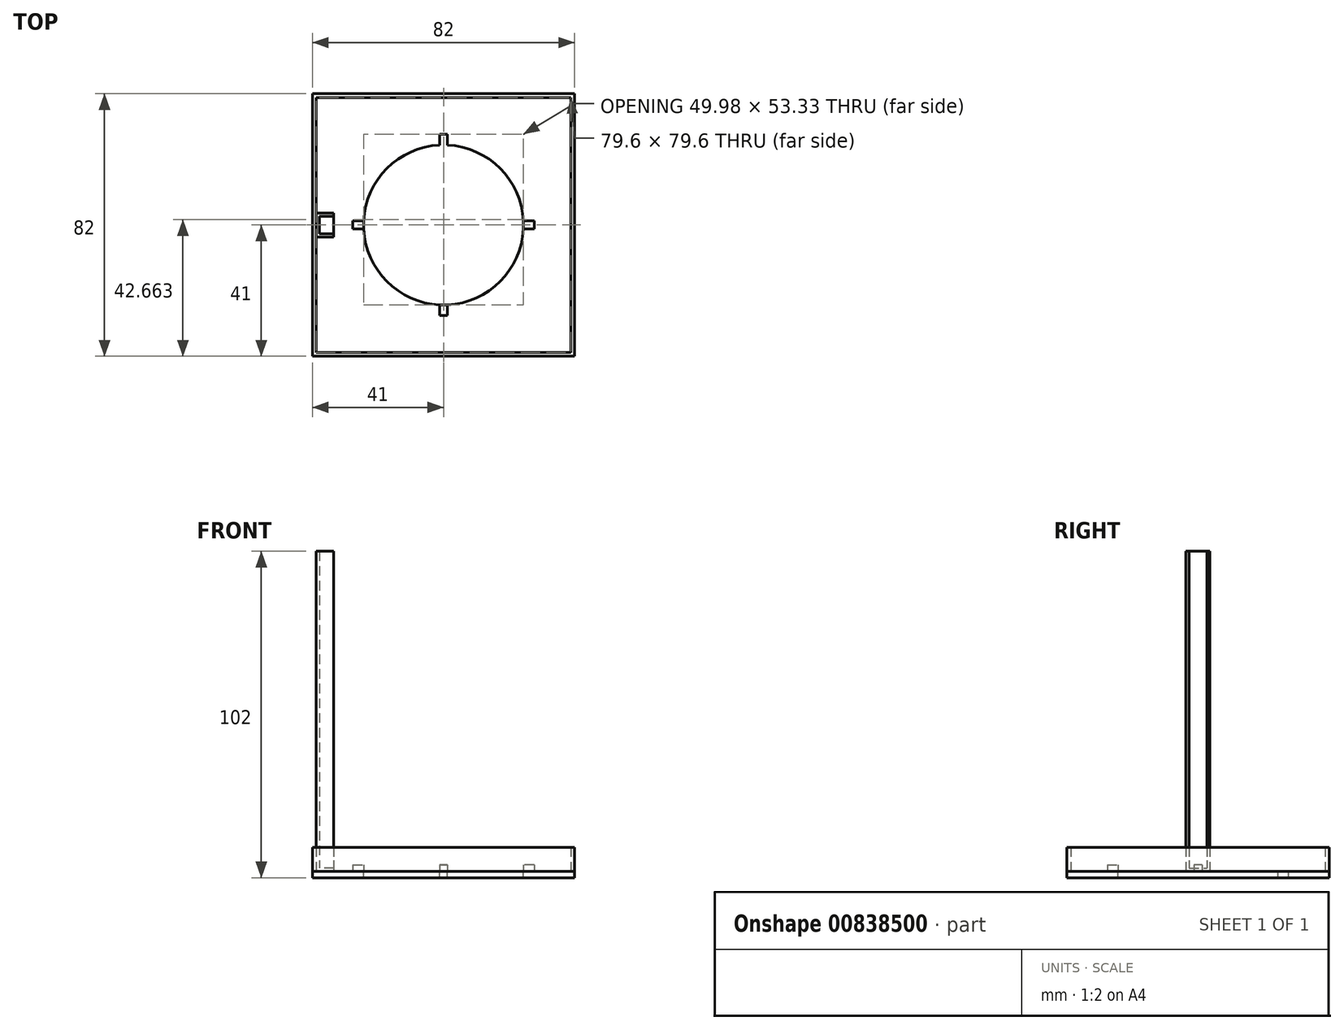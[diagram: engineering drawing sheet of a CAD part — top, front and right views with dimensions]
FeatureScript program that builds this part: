
annotation { "Feature Type Name" : "Feature", "Feature Type Description" : "" }
export const myFeature = defineFeature(function(context is Context, id is Id, definition is map)
    precondition{}
    {
        {
            var Q0;
            Q0=qCreatedBy(makeId("Top.planeOp"),FACE);
            var sketch = newSketch(context, id + "F0", { "sketchPlane" : qUnion([Q0])});
            skCircle(sketch, "E0", {"center": v(0, 0) * mm, "radius": 25 * mm});
            skCircle(sketch, "E1", {"center": v(0, 0) * mm, "radius": 32.8 * mm});
            skLineSegment(sketch, "E2.bottom", {"start": v(-1.25, 28.32) * mm, "end": v(1.25, 28.32) * mm});
            skLineSegment(sketch, "E2.top", {"start": v(-1.25, 21.68) * mm, "end": v(1.25, 21.68) * mm});
            skLineSegment(sketch, "E2.left", {"start": v(-1.25, 28.32) * mm, "end": v(-1.25, 21.68) * mm});
            skLineSegment(sketch, "E2.right", {"start": v(1.25, 28.32) * mm, "end": v(1.25, 21.68) * mm});
            skPoint(sketch, "E2.middle", {"position": v(0, 25) * mm});
            skLineSegment(sketch, "E3.bottom", {"start": v(28.33, 1.25) * mm, "end": v(21.68, 1.25) * mm});
            skLineSegment(sketch, "E3.top", {"start": v(28.33, -1.25) * mm, "end": v(21.68, -1.25) * mm});
            skLineSegment(sketch, "E3.left", {"start": v(28.33, 1.25) * mm, "end": v(28.33, -1.25) * mm});
            skLineSegment(sketch, "E3.right", {"start": v(21.68, 1.25) * mm, "end": v(21.68, -1.25) * mm});
            skPoint(sketch, "E3.middle", {"position": v(25, 0) * mm});
            skLineSegment(sketch, "E4.MirrorCS", {"start": v(1.25, 28.32) * mm, "end": v(-1.25, 28.32) * mm});
            skLineSegment(sketch, "E5.MirrorCS", {"start": v(1.25, 21.68) * mm, "end": v(-1.25, 21.68) * mm});
            skLineSegment(sketch, "E6.MirrorCS", {"start": v(-1.25, -21.68) * mm, "end": v(1.25, -21.68) * mm});
            skLineSegment(sketch, "E7.MirrorCS", {"start": v(-1.25, -28.32) * mm, "end": v(-1.25, -21.68) * mm});
            skLineSegment(sketch, "E8.MirrorCS", {"start": v(1.25, -28.32) * mm, "end": v(-1.25, -28.32) * mm});
            skLineSegment(sketch, "E9.MirrorCS", {"start": v(1.25, -28.32) * mm, "end": v(1.25, -21.68) * mm});
            skLineSegment(sketch, "E10.MirrorCS", {"start": v(-21.68, 1.25) * mm, "end": v(-21.68, -1.25) * mm});
            skLineSegment(sketch, "E11.MirrorCS", {"start": v(-28.33, 1.25) * mm, "end": v(-21.68, 1.25) * mm});
            skLineSegment(sketch, "E12.MirrorCS", {"start": v(-28.33, -1.25) * mm, "end": v(-21.68, -1.25) * mm});
            skLineSegment(sketch, "E13.MirrorCS", {"start": v(-28.33, 1.25) * mm, "end": v(-28.33, -1.25) * mm});
            skPoint(sketch, "E14.middle", {"position": v(-41.79, 0) * mm});
            skCircle(sketch, "E15", {"center": v(0, 0) * mm, "radius": 23.8 * mm});
            skLineSegment(sketch, "E16.bottom", {"start": v(-39.8, 39.8) * mm, "end": v(39.8, 39.8) * mm});
            skLineSegment(sketch, "E16.top", {"start": v(-39.8, -39.8) * mm, "end": v(39.8, -39.8) * mm});
            skLineSegment(sketch, "E16.left", {"start": v(-39.8, 39.8) * mm, "end": v(-39.8, -39.8) * mm});
            skLineSegment(sketch, "E16.right", {"start": v(39.8, 39.8) * mm, "end": v(39.8, -39.8) * mm});
            skLineSegment(sketch, "E17.bottom", {"start": v(-41, 41) * mm, "end": v(41, 41) * mm});
            skLineSegment(sketch, "E17.top", {"start": v(-41, -41) * mm, "end": v(41, -41) * mm});
            skLineSegment(sketch, "E17.left", {"start": v(-41, 41) * mm, "end": v(-41, -41) * mm});
            skLineSegment(sketch, "E17.right", {"start": v(41, 41) * mm, "end": v(41, -41) * mm});
            skLineSegment(sketch, "E18.bottom", {"start": v(-34.3, -3.75) * mm, "end": v(-39.8, -3.75) * mm});
            skLineSegment(sketch, "E18.top", {"start": v(-34.3, 3.75) * mm, "end": v(-39.8, 3.75) * mm});
            skLineSegment(sketch, "E18.left", {"start": v(-34.3, -3.75) * mm, "end": v(-34.3, 3.75) * mm});
            skLineSegment(sketch, "E18.right", {"start": v(-39.8, -3.75) * mm, "end": v(-39.8, 3.75) * mm});
            skPoint(sketch, "E18.middle", {"position": v(-37.05, 0) * mm});
            skSolve(sketch);
        }
        {
            var Q0;
            {var subQ0=sQuery(id+"F0.wireOp",EDGE,"E14.top");var subQ1=sQuery(id+"F0.wireOp",EDGE,"ETdMOg9K-giOR-L7Ai-rbHK-IAAoiEiWwUd0");var subQ2=makeQuery(id+"F0.imprint","INTERSECT",VERTEX,{"derivedFrom":[subQ1,subQ0]});Q0=makeQuery(id+"F0.imprint","IMPRINT",FACE,{"disambiguationData":[TD([[makeQuery(id+"F0.imprint","IMPRINT",EDGE,{"disambiguationData":[TD([[subQ2,1.0]])],"derivedFrom":subQ1}),-1.0]])]});}
            var Q1;
            {var subQ3=sQuery(id+"F0.wireOp",EDGE,"ETdMOg9K-giOR-L7Ai-rbHK-IAAoiEiWwUd0");var subQ5=makeQuery(id+"F0.imprint","INTERSECT",VERTEX,{"derivedFrom":[subQ3,sQuery(id+"F0.wireOp",EDGE,"7CK1xZji-ef6t-rpsp-r9yB-K5cPyd019NKb")]});Q1=makeQuery(id+"F0.imprint","IMPRINT",FACE,{"disambiguationData":[TD([[makeQuery(id+"F0.imprint","IMPRINT",EDGE,{"disambiguationData":[TD([[subQ5,1.0]])],"derivedFrom":subQ3}),-1.0]])]});}
            var Q2;
            {var subQ0=sQuery(id+"F0.wireOp",EDGE,"E7.MirrorCS");var subQ1=sQuery(id+"F0.wireOp",EDGE,"E0");var subQ2=makeQuery(id+"F0.imprint","INTERSECT",VERTEX,{"derivedFrom":[subQ1,subQ0]});Q2=makeQuery(id+"F0.imprint","IMPRINT",FACE,{"disambiguationData":[TD([[makeQuery(id+"F0.imprint","IMPRINT",EDGE,{"disambiguationData":[TD([[subQ2,-1.0]])],"derivedFrom":subQ1}),-1.0]])]});}
            var Q3;
            {var subQ0=sQuery(id+"F0.wireOp",EDGE,"E11.MirrorCS");var subQ1=sQuery(id+"F0.wireOp",EDGE,"E0");var subQ2=makeQuery(id+"F0.imprint","INTERSECT",VERTEX,{"derivedFrom":[subQ1,subQ0]});Q3=makeQuery(id+"F0.imprint","IMPRINT",FACE,{"disambiguationData":[TD([[makeQuery(id+"F0.imprint","IMPRINT",EDGE,{"disambiguationData":[TD([[subQ2,-1.0]])],"derivedFrom":subQ1}),-1.0]])]});}
            var Q4;
            {var subQ0=sQuery(id+"F0.wireOp",EDGE,"E2.right");var subQ1=sQuery(id+"F0.wireOp",EDGE,"E0");var subQ2=makeQuery(id+"F0.imprint","INTERSECT",VERTEX,{"derivedFrom":[subQ1,subQ0]});Q4=makeQuery(id+"F0.imprint","IMPRINT",FACE,{"disambiguationData":[TD([[makeQuery(id+"F0.imprint","IMPRINT",EDGE,{"disambiguationData":[TD([[subQ2,-1.0]])],"derivedFrom":subQ1}),-1.0]])]});}
            var Q5;
            {var subQ0=sQuery(id+"F0.wireOp",EDGE,"E9.MirrorCS");var subQ1=sQuery(id+"F0.wireOp",EDGE,"E0");var subQ2=makeQuery(id+"F0.imprint","INTERSECT",VERTEX,{"derivedFrom":[subQ1,subQ0]});Q5=makeQuery(id+"F0.imprint","IMPRINT",FACE,{"disambiguationData":[TD([[makeQuery(id+"F0.imprint","IMPRINT",EDGE,{"disambiguationData":[TD([[subQ2,1.0]])],"derivedFrom":subQ1}),-1.0]])]});}
            var Q6;
            {var subQ0=sQuery(id+"F0.wireOp",EDGE,"E2.left");var subQ1=sQuery(id+"F0.wireOp",EDGE,"E0");var subQ2=makeQuery(id+"F0.imprint","INTERSECT",VERTEX,{"derivedFrom":[subQ1,subQ0]});Q6=makeQuery(id+"F0.imprint","IMPRINT",FACE,{"disambiguationData":[TD([[makeQuery(id+"F0.imprint","IMPRINT",EDGE,{"disambiguationData":[TD([[subQ2,-1.0]])],"derivedFrom":subQ1}),-1.0]])]});}
            var Q7;
            {var subQ0=sQuery(id+"F0.wireOp",EDGE,"E9.MirrorCS");var subQ1=sQuery(id+"F0.wireOp",EDGE,"E0");var subQ2=makeQuery(id+"F0.imprint","INTERSECT",VERTEX,{"derivedFrom":[subQ1,subQ0]});Q7=makeQuery(id+"F0.imprint","IMPRINT",FACE,{"disambiguationData":[TD([[makeQuery(id+"F0.imprint","IMPRINT",EDGE,{"disambiguationData":[TD([[subQ2,-1.0]])],"derivedFrom":subQ1}),-1.0]])]});}
            var Q8;
            {var subQ0=sQuery(id+"F0.wireOp",EDGE,"E3.top");var subQ1=sQuery(id+"F0.wireOp",EDGE,"E0");var subQ2=makeQuery(id+"F0.imprint","INTERSECT",VERTEX,{"derivedFrom":[subQ1,subQ0]});Q8=makeQuery(id+"F0.imprint","IMPRINT",FACE,{"disambiguationData":[TD([[makeQuery(id+"F0.imprint","IMPRINT",EDGE,{"disambiguationData":[TD([[subQ2,1.0]])],"derivedFrom":subQ1}),-1.0]])]});}
            var Q9;
            {var subQ0=sQuery(id+"F0.wireOp",EDGE,"E12.MirrorCS");var subQ1=sQuery(id+"F0.wireOp",EDGE,"E0");var subQ2=makeQuery(id+"F0.imprint","INTERSECT",VERTEX,{"derivedFrom":[subQ1,subQ0]});Q9=makeQuery(id+"F0.imprint","IMPRINT",FACE,{"disambiguationData":[TD([[makeQuery(id+"F0.imprint","IMPRINT",EDGE,{"disambiguationData":[TD([[subQ2,-1.0]])],"derivedFrom":subQ1}),-1.0]])]});}
            var Q10;
            Q10=makeQuery(id+"F0.imprint","IMPRINT",FACE,{"disambiguationData":[TD([[makeQuery(id+"F0.imprint","IMPRINT",EDGE,{"derivedFrom":sQuery(id+"F0.wireOp",EDGE,"E16.bottom")}),1.0]])]});
            var Q11;
            Q11=sQuery(id+"F0.wireOp",EDGE,"ETdMOg9K-giOR-L7Ai-rbHK-IAAoiEiWwUd0");
            var Q12;
            Q12=sQuery(id+"F0.wireOp",EDGE,"E0");
            extrude(context, id + "F1", {"entities" : qUnion([Q0, Q1, Q2, Q3, Q4, Q5, Q6, Q7, Q8, Q9, Q10]), "surfaceEntities" : qUnion([Q11, Q12]), "depth" : 7.5 * mm, "offsetDistance" : 25 * mm});
        }
        {
            var Q0;
            Q0=makeQuery(id+"F0.imprint","IMPRINT",FACE,{"disambiguationData":[TD([[makeQuery(id+"F0.imprint","IMPRINT",EDGE,{"derivedFrom":sQuery(id+"F0.wireOp",EDGE,"E1")}),-1.0]])]});
            var Q1;
            Q1=makeQuery(id+"F0.imprint","IMPRINT",FACE,{"disambiguationData":[TD([[makeQuery(id+"F0.imprint","IMPRINT",EDGE,{"derivedFrom":sQuery(id+"F0.wireOp",EDGE,"E0")}),-1.0]])]});
            var Q2;
            Q2=makeQuery(id+"F0.imprint","IMPRINT",FACE,{"disambiguationData":[TD([[makeQuery(id+"F0.imprint","IMPRINT",EDGE,{"derivedFrom":sQuery(id+"F0.wireOp",EDGE,"7CK1xZji-ef6t-rpsp-r9yB-K5cPyd019NKb")}),1.0]])]});
            var Q3;
            Q3=makeQuery(id+"F0.imprint","IMPRINT",FACE,{"disambiguationData":[TD([[makeQuery(id+"F0.imprint","IMPRINT",EDGE,{"derivedFrom":sQuery(id+"F0.wireOp",EDGE,"E1")}),1.0]])]});
            var Q4;
            {var subQ5=sQuery(id+"F0.wireOp",EDGE,"E13.MirrorCS");Q4=makeQuery(id+"F0.imprint","IMPRINT",FACE,{"disambiguationData":[TD([[makeQuery(id+"F0.imprint","IMPRINT",EDGE,{"derivedFrom":subQ5}),1.0]])]});}
            var Q5;
            {var subQ5=sQuery(id+"F0.wireOp",EDGE,"E8.MirrorCS");Q5=makeQuery(id+"F0.imprint","IMPRINT",FACE,{"disambiguationData":[TD([[makeQuery(id+"F0.imprint","IMPRINT",EDGE,{"derivedFrom":subQ5}),-1.0]])]});}
            var Q6;
            {var subQ5=sQuery(id+"F0.wireOp",EDGE,"E4.MirrorCS");Q6=makeQuery(id+"F0.imprint","IMPRINT",FACE,{"disambiguationData":[TD([[makeQuery(id+"F0.imprint","IMPRINT",EDGE,{"derivedFrom":subQ5}),1.0]])]});}
            var Q7;
            {var subQ5=sQuery(id+"F0.wireOp",EDGE,"E3.left");Q7=makeQuery(id+"F0.imprint","IMPRINT",FACE,{"disambiguationData":[TD([[makeQuery(id+"F0.imprint","IMPRINT",EDGE,{"derivedFrom":subQ5}),-1.0]])]});}
            var Q8;
            {var subQ0=sQuery(id+"F0.wireOp",EDGE,"E14.top");var subQ1=sQuery(id+"F0.wireOp",EDGE,"ETdMOg9K-giOR-L7Ai-rbHK-IAAoiEiWwUd0");var subQ2=makeQuery(id+"F0.imprint","INTERSECT",VERTEX,{"derivedFrom":[subQ1,subQ0]});Q8=makeQuery(id+"F0.imprint","IMPRINT",FACE,{"disambiguationData":[TD([[makeQuery(id+"F0.imprint","IMPRINT",EDGE,{"disambiguationData":[TD([[subQ2,1.0]])],"derivedFrom":subQ1}),-1.0]])]});}
            var Q9;
            {var subQ1=sQuery(id+"F0.wireOp",EDGE,"aaf08cbb-e0e6-44e5-a82d-b8a05a9542510.MirrorCS");Q9=makeQuery(id+"F0.imprint","IMPRINT",FACE,{"disambiguationData":[TD([[makeQuery(id+"F0.imprint","IMPRINT",EDGE,{"derivedFrom":subQ1}),1.0]])]});}
            var Q10;
            {var subQ0=sQuery(id+"F0.wireOp",EDGE,"SpKwcO3M-pOnQ-yAnI-ckbO-jszkQa1rbotf.top");Q10=makeQuery(id+"F0.imprint","IMPRINT",FACE,{"disambiguationData":[TD([[makeQuery(id+"F0.imprint","IMPRINT",EDGE,{"derivedFrom":subQ0}),-1.0]])]});}
            var Q11;
            {var subQ1=sQuery(id+"F0.wireOp",EDGE,"SpKwcO3M-pOnQ-yAnI-ckbO-jszkQa1rbotf.bottom");Q11=makeQuery(id+"F0.imprint","IMPRINT",FACE,{"disambiguationData":[TD([[makeQuery(id+"F0.imprint","IMPRINT",EDGE,{"derivedFrom":subQ1}),1.0]])]});}
            var Q12;
            {var subQ0=sQuery(id+"F0.wireOp",EDGE,"7CK1xZji-ef6t-rpsp-r9yB-K5cPyd019NKb");var subQ1=sQuery(id+"F0.wireOp",EDGE,"ETdMOg9K-giOR-L7Ai-rbHK-IAAoiEiWwUd0");var subQ2=makeQuery(id+"F0.imprint","INTERSECT",VERTEX,{"derivedFrom":[subQ1,subQ0]});Q12=makeQuery(id+"F0.imprint","IMPRINT",FACE,{"disambiguationData":[TD([[makeQuery(id+"F0.imprint","IMPRINT",EDGE,{"disambiguationData":[TD([[subQ2,-1.0]])],"derivedFrom":subQ1}),1.0]])]});}
            var Q13;
            {var subQ0=sQuery(id+"F0.wireOp",EDGE,"7CK1xZji-ef6t-rpsp-r9yB-K5cPyd019NKb");var subQ1=sQuery(id+"F0.wireOp",EDGE,"ETdMOg9K-giOR-L7Ai-rbHK-IAAoiEiWwUd0");var subQ2=makeQuery(id+"F0.imprint","INTERSECT",VERTEX,{"derivedFrom":[subQ1,subQ0]});Q13=makeQuery(id+"F0.imprint","IMPRINT",FACE,{"disambiguationData":[TD([[makeQuery(id+"F0.imprint","IMPRINT",EDGE,{"disambiguationData":[TD([[subQ2,1.0]])],"derivedFrom":subQ1}),1.0]])]});}
            var Q14;
            {var subQ0=sQuery(id+"F0.wireOp",EDGE,"7e1316c8-d3c2-4bb1-b3af-9022fed48cfa0.MirrorCS");Q14=makeQuery(id+"F0.imprint","IMPRINT",FACE,{"disambiguationData":[TD([[makeQuery(id+"F0.imprint","IMPRINT",EDGE,{"derivedFrom":subQ0}),-1.0]])]});}
            var Q15;
            {var subQ3=sQuery(id+"F0.wireOp",EDGE,"ETdMOg9K-giOR-L7Ai-rbHK-IAAoiEiWwUd0");var subQ8=makeQuery(id+"F0.imprint","INTERSECT",VERTEX,{"derivedFrom":[subQ3,sQuery(id+"F0.wireOp",EDGE,"7CK1xZji-ef6t-rpsp-r9yB-K5cPyd019NKb")]});Q15=makeQuery(id+"F0.imprint","IMPRINT",FACE,{"disambiguationData":[TD([[makeQuery(id+"F0.imprint","IMPRINT",EDGE,{"disambiguationData":[TD([[subQ8,1.0]])],"derivedFrom":subQ3}),-1.0]])]});}
            var Q16;
            {var subQ1=sQuery(id+"F0.wireOp",EDGE,"aaf08cbb-e0e6-44e5-a82d-b8a05a9542510.MirrorCS");Q16=makeQuery(id+"F0.imprint","IMPRINT",FACE,{"disambiguationData":[TD([[makeQuery(id+"F0.imprint","IMPRINT",EDGE,{"derivedFrom":subQ1}),1.0]])]});}
            var Q17;
            Q17=makeQuery(id+"F0.imprint","IMPRINT",FACE,{"disambiguationData":[TD([[makeQuery(id+"F0.imprint","IMPRINT",EDGE,{"derivedFrom":sQuery(id+"F0.wireOp",EDGE,"E1")}),-1.0]])]});
            var Q18;
            {var subQ0=sQuery(id+"F0.wireOp",EDGE,"SpKwcO3M-pOnQ-yAnI-ckbO-jszkQa1rbotf.right");var subQ1=sQuery(id+"F0.wireOp",EDGE,"7CK1xZji-ef6t-rpsp-r9yB-K5cPyd019NKb");var subQ2=makeQuery(id+"F0.imprint","INTERSECT",VERTEX,{"derivedFrom":[subQ1,subQ0]});Q18=makeQuery(id+"F0.imprint","IMPRINT",FACE,{"disambiguationData":[TD([[makeQuery(id+"F0.imprint","IMPRINT",EDGE,{"disambiguationData":[TD([[subQ2,1.0]])],"derivedFrom":subQ1}),1.0]])]});}
            var Q19;
            {var subQ1=sQuery(id+"F0.wireOp",EDGE,"SpKwcO3M-pOnQ-yAnI-ckbO-jszkQa1rbotf.bottom");Q19=makeQuery(id+"F0.imprint","IMPRINT",FACE,{"disambiguationData":[TD([[makeQuery(id+"F0.imprint","IMPRINT",EDGE,{"derivedFrom":subQ1}),-1.0]])]});}
            var Q20;
            Q20=makeQuery(id+"F0.imprint","IMPRINT",FACE,{"disambiguationData":[TD([[makeQuery(id+"F0.imprint","IMPRINT",EDGE,{"derivedFrom":sQuery(id+"F0.wireOp",EDGE,"E16.bottom")}),1.0]])]});
            var Q21;
            Q21=makeQuery(id+"F0.imprint","IMPRINT",FACE,{"disambiguationData":[TD([[makeQuery(id+"F0.imprint","IMPRINT",EDGE,{"derivedFrom":sQuery(id+"F0.wireOp",EDGE,"E18.bottom")}),-1.0]])]});
            var Q22;
            {var subQ0=sQuery(id+"F0.wireOp",EDGE,"E9.MirrorCS");var subQ1=sQuery(id+"F0.wireOp",EDGE,"E0");var subQ2=makeQuery(id+"F0.imprint","INTERSECT",VERTEX,{"derivedFrom":[subQ1,subQ0]});Q22=makeQuery(id+"F0.imprint","IMPRINT",FACE,{"disambiguationData":[TD([[makeQuery(id+"F0.imprint","IMPRINT",EDGE,{"disambiguationData":[TD([[subQ2,1.0]])],"derivedFrom":subQ1}),-1.0]])]});}
            var Q23;
            {var subQ0=sQuery(id+"F0.wireOp",EDGE,"E9.MirrorCS");var subQ1=sQuery(id+"F0.wireOp",EDGE,"E0");var subQ2=makeQuery(id+"F0.imprint","INTERSECT",VERTEX,{"derivedFrom":[subQ1,subQ0]});Q23=makeQuery(id+"F0.imprint","IMPRINT",FACE,{"disambiguationData":[TD([[makeQuery(id+"F0.imprint","IMPRINT",EDGE,{"disambiguationData":[TD([[subQ2,-1.0]])],"derivedFrom":subQ1}),-1.0]])]});}
            var Q24;
            {var subQ0=sQuery(id+"F0.wireOp",EDGE,"E7.MirrorCS");var subQ1=sQuery(id+"F0.wireOp",EDGE,"E0");var subQ2=makeQuery(id+"F0.imprint","INTERSECT",VERTEX,{"derivedFrom":[subQ1,subQ0]});Q24=makeQuery(id+"F0.imprint","IMPRINT",FACE,{"disambiguationData":[TD([[makeQuery(id+"F0.imprint","IMPRINT",EDGE,{"disambiguationData":[TD([[subQ2,-1.0]])],"derivedFrom":subQ1}),-1.0]])]});}
            var Q25;
            {var subQ0=sQuery(id+"F0.wireOp",EDGE,"E3.top");var subQ1=sQuery(id+"F0.wireOp",EDGE,"E0");var subQ2=makeQuery(id+"F0.imprint","INTERSECT",VERTEX,{"derivedFrom":[subQ1,subQ0]});Q25=makeQuery(id+"F0.imprint","IMPRINT",FACE,{"disambiguationData":[TD([[makeQuery(id+"F0.imprint","IMPRINT",EDGE,{"disambiguationData":[TD([[subQ2,1.0]])],"derivedFrom":subQ1}),-1.0]])]});}
            var Q26;
            {var subQ0=sQuery(id+"F0.wireOp",EDGE,"E2.right");var subQ1=sQuery(id+"F0.wireOp",EDGE,"E0");var subQ2=makeQuery(id+"F0.imprint","INTERSECT",VERTEX,{"derivedFrom":[subQ1,subQ0]});Q26=makeQuery(id+"F0.imprint","IMPRINT",FACE,{"disambiguationData":[TD([[makeQuery(id+"F0.imprint","IMPRINT",EDGE,{"disambiguationData":[TD([[subQ2,-1.0]])],"derivedFrom":subQ1}),-1.0]])]});}
            var Q27;
            {var subQ0=sQuery(id+"F0.wireOp",EDGE,"E2.left");var subQ1=sQuery(id+"F0.wireOp",EDGE,"E0");var subQ2=makeQuery(id+"F0.imprint","INTERSECT",VERTEX,{"derivedFrom":[subQ1,subQ0]});Q27=makeQuery(id+"F0.imprint","IMPRINT",FACE,{"disambiguationData":[TD([[makeQuery(id+"F0.imprint","IMPRINT",EDGE,{"disambiguationData":[TD([[subQ2,-1.0]])],"derivedFrom":subQ1}),-1.0]])]});}
            var Q28;
            {var subQ0=sQuery(id+"F0.wireOp",EDGE,"E11.MirrorCS");var subQ1=sQuery(id+"F0.wireOp",EDGE,"E0");var subQ2=makeQuery(id+"F0.imprint","INTERSECT",VERTEX,{"derivedFrom":[subQ1,subQ0]});Q28=makeQuery(id+"F0.imprint","IMPRINT",FACE,{"disambiguationData":[TD([[makeQuery(id+"F0.imprint","IMPRINT",EDGE,{"disambiguationData":[TD([[subQ2,-1.0]])],"derivedFrom":subQ1}),-1.0]])]});}
            var Q29;
            {var subQ0=sQuery(id+"F0.wireOp",EDGE,"E12.MirrorCS");var subQ1=sQuery(id+"F0.wireOp",EDGE,"E0");var subQ2=makeQuery(id+"F0.imprint","INTERSECT",VERTEX,{"derivedFrom":[subQ1,subQ0]});Q29=makeQuery(id+"F0.imprint","IMPRINT",FACE,{"disambiguationData":[TD([[makeQuery(id+"F0.imprint","IMPRINT",EDGE,{"disambiguationData":[TD([[subQ2,-1.0]])],"derivedFrom":subQ1}),-1.0]])]});}
            var Q30;
            Q30=sQuery(id+"F0.wireOp",EDGE,"ETdMOg9K-giOR-L7Ai-rbHK-IAAoiEiWwUd0");
            var Q31;
            Q31=sQuery(id+"F0.wireOp",EDGE,"E0");
            extrude(context, id + "F2", {"entities" : qUnion([Q0, Q1, Q2, Q3, Q4, Q5, Q6, Q7, Q8, Q9, Q10, Q11, Q12, Q13, Q14, Q15, Q16, Q17, Q18, Q19, Q20, Q21, Q22, Q23, Q24, Q25, Q26, Q27, Q28, Q29]), "surfaceOperationType" : NewSurfaceOperationType.ADD, "surfaceEntities" : qUnion([Q30, Q31]), "oppositeDirection" : true, "depth" : 2 * mm, "offsetDistance" : 25 * mm});
        }
        {
            var Q0;
            {var subQ5=sQuery(id+"F0.wireOp",EDGE,"E13.MirrorCS");Q0=makeQuery(id+"F0.imprint","IMPRINT",FACE,{"disambiguationData":[TD([[makeQuery(id+"F0.imprint","IMPRINT",EDGE,{"derivedFrom":subQ5}),1.0]])]});}
            var Q1;
            {var subQ5=sQuery(id+"F0.wireOp",EDGE,"E4.MirrorCS");Q1=makeQuery(id+"F0.imprint","IMPRINT",FACE,{"disambiguationData":[TD([[makeQuery(id+"F0.imprint","IMPRINT",EDGE,{"derivedFrom":subQ5}),1.0]])]});}
            var Q2;
            {var subQ5=sQuery(id+"F0.wireOp",EDGE,"E3.left");Q2=makeQuery(id+"F0.imprint","IMPRINT",FACE,{"disambiguationData":[TD([[makeQuery(id+"F0.imprint","IMPRINT",EDGE,{"derivedFrom":subQ5}),-1.0]])]});}
            var Q3;
            {var subQ5=sQuery(id+"F0.wireOp",EDGE,"E8.MirrorCS");Q3=makeQuery(id+"F0.imprint","IMPRINT",FACE,{"disambiguationData":[TD([[makeQuery(id+"F0.imprint","IMPRINT",EDGE,{"derivedFrom":subQ5}),-1.0]])]});}
            extrude(context, id + "F3", {"entities" : qUnion([Q0, Q1, Q2, Q3]), "depth" : 2 * mm, "offsetDistance" : 25 * mm});
        }
        {
            var Q0;
            Q0=makeQuery(id+"F0.imprint","IMPRINT",FACE,{"disambiguationData":[TD([[makeQuery(id+"F0.imprint","IMPRINT",EDGE,{"derivedFrom":sQuery(id+"F0.wireOp",EDGE,"E18.bottom")}),-1.0]])]});
            extrude(context, id + "F4", {"entities" : qUnion([Q0]), "depth" : 100 * mm, "offsetDistance" : 25 * mm});
        }
        {
            var Q0;
            Q0=makeQuery(id+"F4.opExtrude","CAP_FACE",FACE,{"disambiguationData":[OSD([sQuery(id+"F0.wireOp",EDGE,"E18.bottom"),sQuery(id+"F0.wireOp",EDGE,"E18.top"),sQuery(id+"F0.wireOp",EDGE,"E18.left"),sQuery(id+"F0.wireOp",EDGE,"E18.right")])],"isStart":false});
            var Q1;
            Q1=makeQuery(id+"F4.opExtrude","SWEPT_FACE",FACE,{"disambiguationData":[OSD([sQuery(id+"F0.wireOp",EDGE,"E18.left")])]});
            shell(context, id + "F5", {"entities" : qUnion([Q0, Q1]), "thickness" : 1 * mm});
        }
    });
